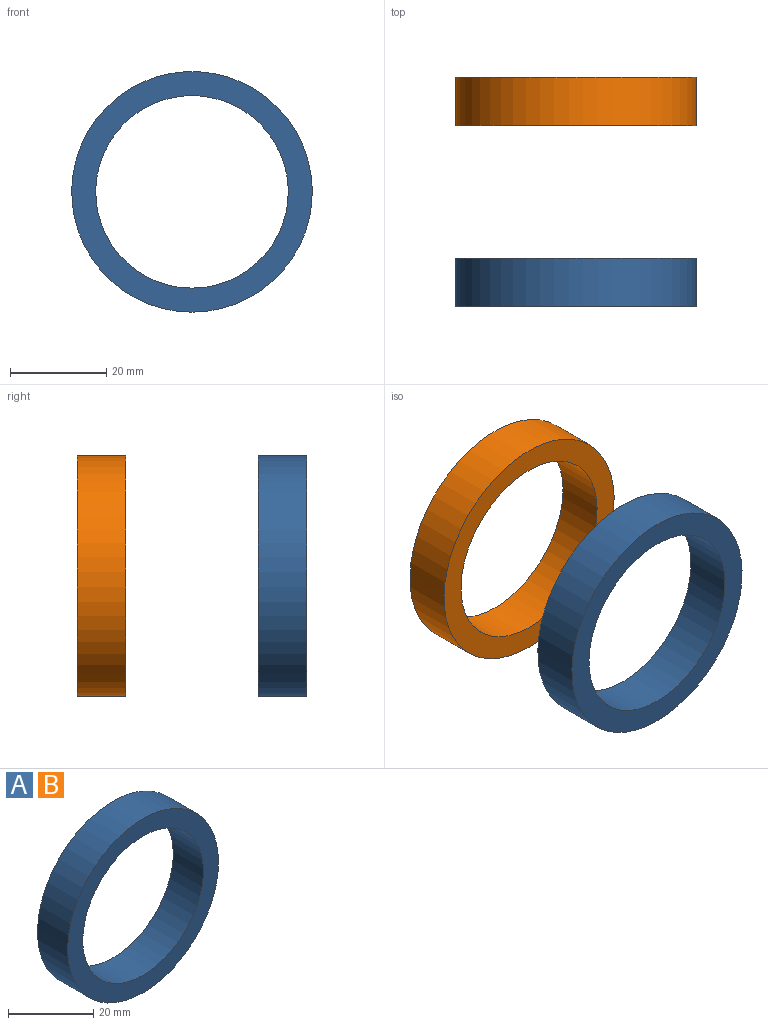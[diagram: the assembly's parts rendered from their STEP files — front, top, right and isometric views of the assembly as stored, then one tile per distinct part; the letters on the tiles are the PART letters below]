
ASSEMBLY  parts=2 mates=1
PART A: 4 faces, bbox 50x10x50 mm
  f0: cylinder r=20mm len=40mm, axis (0,1,0), area 1256.6mm2, adj f2,f3
  f1: cylinder r=25mm len=50mm, axis (0,1,0), area 1570.8mm2, adj f2,f3
  f2: plane 50x50mm, normal (0,-1,0), area 706.9mm2, adj f0,f1
  f3: plane 50x50mm, normal (0,1,0), area 706.9mm2, adj f0,f1
PART B: same geometry as A
PLACE A t=(0,-37.59,0)mm
PLACE B at identity fixed
MATE slider B.f1 <-> A.f1  axis (0,1,0) through (0,-10,0)mm
